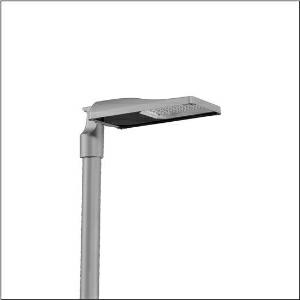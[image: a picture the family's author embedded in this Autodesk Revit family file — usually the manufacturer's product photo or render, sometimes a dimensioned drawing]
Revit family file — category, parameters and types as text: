
# Revit family: streetlight_sl_31_mini___st1_0a_5xh2d31a08ja_70b8
name_source: partatom
category: Lighting Fixtures
units: mm (PartAtom-declared; Revit-internal decimal feet)

## family parameters
Cut with Voids When Loaded = No
Host = Face
Light Source = No
Part Type = Normal
Room Calculation Point = No
Round Connector Dimension = Use Diameter
Shared = No

## types (1)
- --- (1 x LED, 12140 lm, 81.1 W, 3000K)
    Apparent Load = 81 VA
    CIE Flux Codes = 40 73 97 100 100
    Color Rendering = 70
    Color Temperature = 3000K
    Default Elevation = 1800 mm
    Description = Streetlight SL 31 mini Easy, Desk-Remote mast luminaire for post-top, side-entry; light control with lens of PMMA; light distribution: ST1.0a, direct asymmetric distribution, for standard-compliant lighting for roads and squares; LED: luminous flux: 12.140lm, light colour: 730, colour temperature: 3000K; luminous efficacy: 149,7lm/W; control: pre-setting: linear dimming characteristic, flexible luminous flux parameterisation, time-dependent luminous flux control, constant luminous flux control, intelligent temperature release in ECG and LED module, overheat protection; luminaire housing, of diecast aluminium, Siteco® metallic grey (DB 702S), corrosivity category C5 high according to DIN EN ISO 12944; cover of toughened safety glass, transparent, mast flange of diecast aluminium, Siteco® metallic grey (DB 702S), spigot size: 76/60mm, mast flange included unmounted; with cable H07RN-F 2x 1.5mm², cable length: 10,5m, connection cable pre-assembled; mains connection: 220..240V, AC, 50/60Hz; power consumption (at start of service life): 81,1W / (at end of service life): 88,3W / (with reduced operation 50%): 36,4W; protection rating (complete): IP66; insulation class (complete): insulation class II (safety insulation); impact resistance: IK10; certification: CE, ENEC, ENEC+, VDE, UKCA; permissible operating ambient temperature for outdoor applications: -40..+50°C; packaging unit: 1 piece

Light Distribution: ST1.0a
    Height = 76 mm
    Lamp = 1 x LED
    Lamp Light Flux = 12140 lm
    Lamp Power = 81.1 W
    Lamp count = 1
    Length = 547 mm
    Luminous efficacy = 150 lm/W
    Manufacturer = Siteco
    ModVariant = No
    Model = 5XH2D31A08JA
    Number of Poles = 1
    OnlyDefault = Yes
    Power Factor = 1
    Product Name = Streetlight SL 31 mini | ST1.0a
    Product group = mast luminaire | pylon top
    ProductGroupID = 6100
    Protection Class = Protection class II
    Protection Degree = IP 66
    RLX_Detail_Level = 1
    RLX_Emergency_Light_Flux = 0 lm
    RLX_Emergency_Type = 0
    RLX_Emergency_Type_DB = No
    RlxData = <blob elided: 39637 chars, md5=ee813cc1>
    Socket = socket
    Standby Power = 0 W
    System Light Flux = 12140 lm
    System Power = 81 W
    Type Comments = factory setting: luminous flux: 100 % | dim-lin: 254 | 860 mA
    Type Image = l_1300326.jpg
    URL = http://relux.com
    VarID = @adj_051166
    Voltage = 0 V
    Weight = 0.00 kg
    Width = 265 mm

## geometry (parser evidence)
native form markers: Blend x4, Sweep x11
no freeform markers — native parametric forms only
